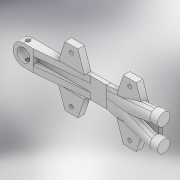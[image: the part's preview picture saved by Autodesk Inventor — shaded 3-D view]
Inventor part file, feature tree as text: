
AUTODESK INVENTOR PART (.ipt)
format: ipt  version: 2018.2 (Build 222227000, 227)  size: 364,032 bytes
history: native  units: mm
features: sketch x8, extrude x7, projected_geometry x3, plane x2, loft x2, mirror x2
ambient origin geometry x8: Origin, YZ Plane, XZ Plane, XY Plane, X Axis, Y Axis, Z Axis, Center Point
bodies: Solid1 (feature_tree)
feature tree (24):
  sketch  "Sketch1"  dims[d0=10.0mm d2=3.0mm]
  extrude  "Extrusion1"  Depth=3.0mm
  extrude  "Extrusion2"  Depth=16.0mm
  plane  "Work Plane1"
  extrude  "Extrusion3"  Depth=3.0mm TaperAngle=0.0deg
  sketch  "Sketch3"  dims[d5=3.0mm d6=0.0mm d7=4.0mm d8=0.0mm]
  plane  "Work Plane2"
  sketch  "Sketch4"  dims[d9=6.0mm d10=9.525mm]
  loft  "Loft2"
  loft  "Loft3"
  extrude  "Extrusion4"  Depth=5.0mm TaperAngle=0.0deg
  extrude  "Extrusion5"  Depth=5.0mm
  mirror  "Mirror1"
  extrude  "Extrusion6"  Depth=5.0mm
  sketch  "Sketch14"  dims[d26=5.0mm d27=0.0mm d62=20.0mm d63=10.0mm d64=20.0mm d65=5.0mm d66=5.0mm d67=3.0mm d68=3.0mm d69=45.0mm d70=18.0mm d71=5.0mm d72=35.0mm d75=18.0mm d94=0.0mm d95=90.0deg d96=0.0mm d97=90.0deg d98=0.0mm d99=90.0deg d100=0.0mm d101=90.0deg d102=5.0mm d103=0.0mm]
  extrude  "Extrusion13"  Depth=10.0mm
  mirror  "Mirror4"
  sketch  "Sketch2"  dims[d3=100.0mm d4=16.0mm]
  sketch  "Sketch6"  dims[d11=6.0mm d12=0.0mm d13=-40.0mm]
  sketch  "Sketch7"  dims[d20=40.0mm d21=5.0mm d22=0.0mm]
  projected_geometry  "Projected Loop2"
  sketch  "Sketch8"  dims[d23=5.0mm d24=0.0mm d25=3.2mm]
  projected_geometry  "Projected Loop3"
  projected_geometry  "Projected Loop4"
